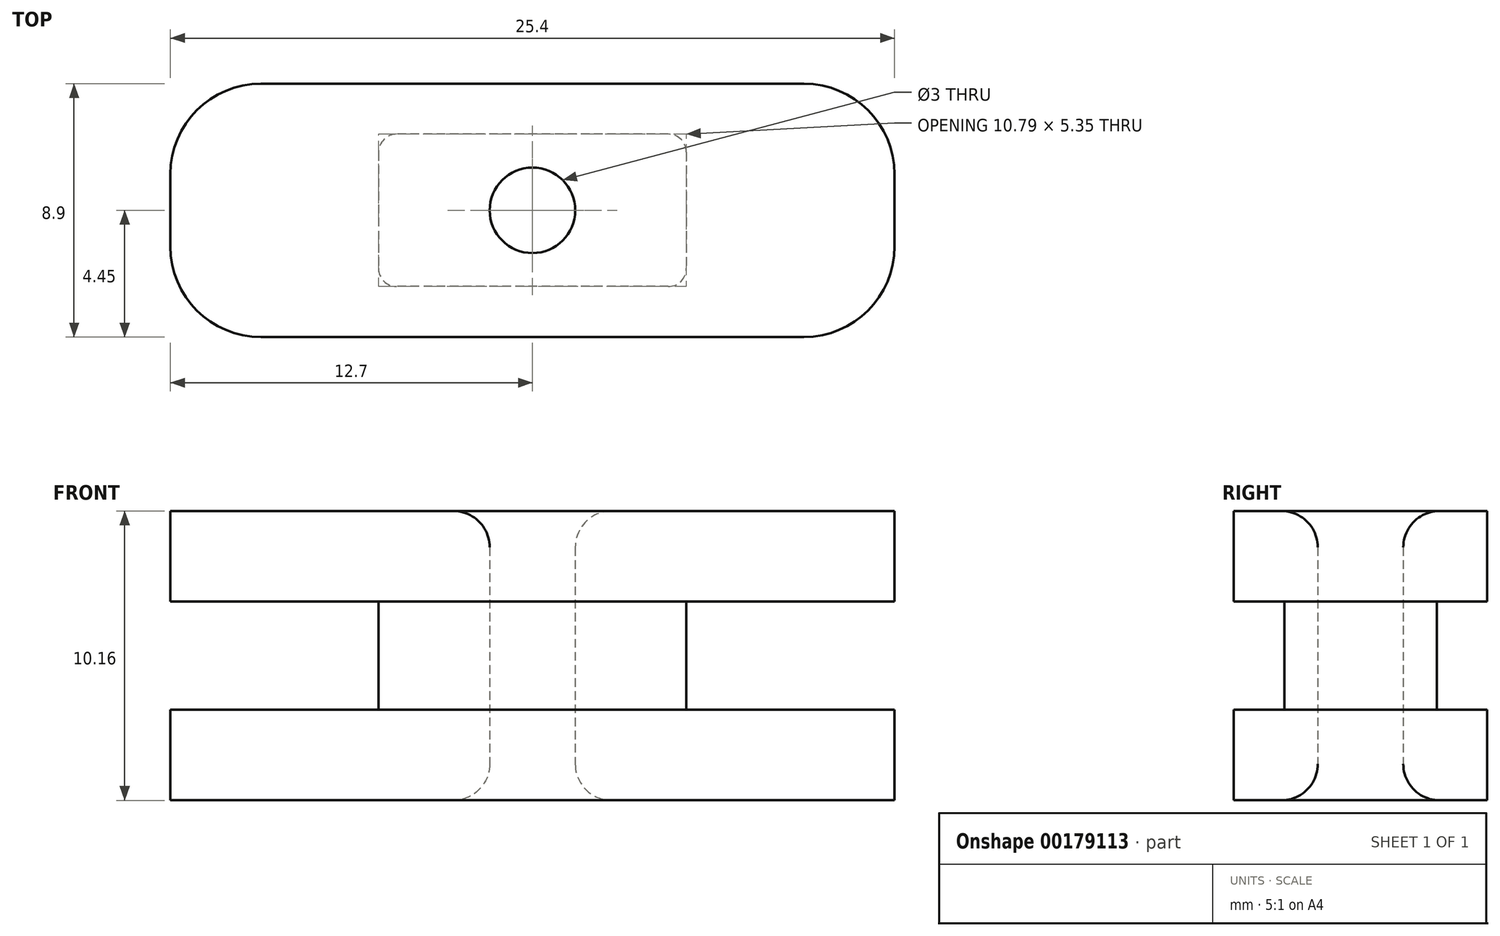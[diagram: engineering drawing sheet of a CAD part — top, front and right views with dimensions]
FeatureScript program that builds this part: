
annotation { "Feature Type Name" : "Feature", "Feature Type Description" : "" }
export const myFeature = defineFeature(function(context is Context, id is Id, definition is map)
    precondition{}
    {
        {
            var Q0;
            Q0=qCreatedBy(makeId("Top.planeOp"),FACE);
            var sketch = newSketch(context, id + "F0", { "sketchPlane" : qUnion([Q0])});
            skLineSegment(sketch, "E0.bottom", {"start": v(9.53, 4.45) * mm, "end": v(-9.53, 4.44) * mm});
            skLineSegment(sketch, "E0.top", {"start": v(9.53, -4.44) * mm, "end": v(-9.53, -4.45) * mm});
            skLineSegment(sketch, "E0.left", {"start": v(12.7, 1.27) * mm, "end": v(12.7, -1.27) * mm});
            skLineSegment(sketch, "E0.right", {"start": v(-12.7, 1.27) * mm, "end": v(-12.7, -1.27) * mm});
            skPoint(sketch, "E0.middle", {"position": v(0, 0) * mm});
            skLineSegment(sketch, "E1.bottom", {"start": v(4.76, 2.67) * mm, "end": v(-4.76, 2.67) * mm});
            skLineSegment(sketch, "E1.top", {"start": v(4.76, -2.67) * mm, "end": v(-4.76, -2.67) * mm});
            skLineSegment(sketch, "E1.left", {"start": v(5.4, 2.04) * mm, "end": v(5.4, -2.04) * mm});
            skLineSegment(sketch, "E1.right", {"start": v(-5.4, 2.04) * mm, "end": v(-5.4, -2.04) * mm});
            skPoint(sketch, "E2.visualSharp", {"position": v(-5.4, 2.67) * mm});
            skArc(sketch, "E2.filletArc", {"start": v(-4.76, 2.67) * mm, "mid": v(-5.21, 2.49) * mm, "end": v(-5.4, 2.04) * mm});
            skPoint(sketch, "E3.visualSharp", {"position": v(-5.4, -2.67) * mm});
            skArc(sketch, "E3.filletArc", {"start": v(-5.4, -2.04) * mm, "mid": v(-5.21, -2.49) * mm, "end": v(-4.76, -2.67) * mm});
            skPoint(sketch, "E4.visualSharp", {"position": v(5.4, -2.67) * mm});
            skArc(sketch, "E4.filletArc", {"start": v(4.76, -2.67) * mm, "mid": v(5.21, -2.49) * mm, "end": v(5.4, -2.04) * mm});
            skPoint(sketch, "E5.visualSharp", {"position": v(5.4, 2.67) * mm});
            skArc(sketch, "E5.filletArc", {"start": v(5.4, 2.04) * mm, "mid": v(5.21, 2.49) * mm, "end": v(4.76, 2.67) * mm});
            skCircle(sketch, "E6", {"center": v(0, 0) * mm, "radius": 1.5 * mm});
            skPoint(sketch, "E7.visualSharp", {"position": v(-12.7, 4.44) * mm});
            skArc(sketch, "E7.filletArc", {"start": v(-9.53, 4.44) * mm, "mid": v(-11.77, 3.52) * mm, "end": v(-12.7, 1.27) * mm});
            skPoint(sketch, "E8.visualSharp", {"position": v(-12.7, -4.45) * mm});
            skArc(sketch, "E8.filletArc", {"start": v(-12.7, -1.27) * mm, "mid": v(-11.77, -3.52) * mm, "end": v(-9.53, -4.45) * mm});
            skPoint(sketch, "E9.visualSharp", {"position": v(12.7, 4.45) * mm});
            skArc(sketch, "E9.filletArc", {"start": v(12.7, 1.27) * mm, "mid": v(11.77, 3.52) * mm, "end": v(9.53, 4.45) * mm});
            skPoint(sketch, "E10.visualSharp", {"position": v(12.7, -4.44) * mm});
            skArc(sketch, "E10.filletArc", {"start": v(9.53, -4.44) * mm, "mid": v(11.77, -3.52) * mm, "end": v(12.7, -1.27) * mm});
            skSolve(sketch);
        }
        {
            var Q0;
            Q0=makeQuery(id+"F0.imprint","IMPRINT",FACE,{"disambiguationData":[TD([[makeQuery(id+"F0.imprint","IMPRINT",EDGE,{"derivedFrom":sQuery(id+"F0.wireOp",EDGE,"E1.bottom")}),1.0]])]});
            extrude(context, id + "F1", {"entities" : qUnion([Q0]), "depth" : 3.8 * mm});
        }
        {
            var Q0;
            Q0 = qSketchRegion(id + "F0", true);
            var Q1;
            Q1=makeQuery(id+"F1.opExtrude","CAP_FACE",FACE,{"disambiguationData":[OSD([sQuery(id+"F0.wireOp",EDGE,"E1.bottom"),sQuery(id+"F0.wireOp",EDGE,"E1.top"),sQuery(id+"F0.wireOp",EDGE,"E1.left"),sQuery(id+"F0.wireOp",EDGE,"E1.right"),sQuery(id+"F0.wireOp",EDGE,"E2.filletArc"),sQuery(id+"F0.wireOp",EDGE,"E3.filletArc"),sQuery(id+"F0.wireOp",EDGE,"E4.filletArc"),sQuery(id+"F0.wireOp",EDGE,"E5.filletArc"),sQuery(id+"F0.wireOp",EDGE,"E6")])],"isStart":true});
            extrude(context, id + "F2", {"entities" : qUnion([Q0, Q1]), "operationType" : NewBodyOperationType.ADD, "oppositeDirection" : true, "depth" : 3.17 * mm});
        }
        {
            var Q0;
            Q0=makeQuery(id+"F1.opExtrude","CAP_FACE",FACE,{"disambiguationData":[OSD([sQuery(id+"F0.wireOp",EDGE,"E1.bottom"),sQuery(id+"F0.wireOp",EDGE,"E1.top"),sQuery(id+"F0.wireOp",EDGE,"E1.left"),sQuery(id+"F0.wireOp",EDGE,"E1.right"),sQuery(id+"F0.wireOp",EDGE,"E2.filletArc"),sQuery(id+"F0.wireOp",EDGE,"E3.filletArc"),sQuery(id+"F0.wireOp",EDGE,"E4.filletArc"),sQuery(id+"F0.wireOp",EDGE,"E5.filletArc"),sQuery(id+"F0.wireOp",EDGE,"E6")])],"isStart":false});
            var sketch = newSketch(context, id + "F3", { "sketchPlane" : qUnion([Q0])});
            skLineSegment(sketch, "E11.bottom", {"start": v(9.53, 4.44) * mm, "end": v(-9.53, 4.45) * mm});
            skLineSegment(sketch, "E11.top", {"start": v(9.53, -4.45) * mm, "end": v(-9.53, -4.45) * mm});
            skLineSegment(sketch, "E11.left", {"start": v(12.7, 1.27) * mm, "end": v(12.7, -1.27) * mm});
            skLineSegment(sketch, "E11.right", {"start": v(-12.7, 1.27) * mm, "end": v(-12.7, -1.27) * mm});
            skPoint(sketch, "E11.middle", {"position": v(0, 0) * mm});
            skCircle(sketch, "E12", {"center": v(0, 0) * mm, "radius": 1.5 * mm});
            skPoint(sketch, "E13.visualSharp", {"position": v(-12.7, 4.45) * mm});
            skArc(sketch, "E13.filletArc", {"start": v(-9.53, 4.45) * mm, "mid": v(-11.77, 3.52) * mm, "end": v(-12.7, 1.27) * mm});
            skPoint(sketch, "E14.visualSharp", {"position": v(-12.7, -4.44) * mm});
            skArc(sketch, "E14.filletArc", {"start": v(-12.7, -1.27) * mm, "mid": v(-11.77, -3.52) * mm, "end": v(-9.53, -4.45) * mm});
            skPoint(sketch, "E15.visualSharp", {"position": v(12.7, 4.44) * mm});
            skArc(sketch, "E15.filletArc", {"start": v(12.7, 1.27) * mm, "mid": v(11.77, 3.52) * mm, "end": v(9.53, 4.44) * mm});
            skPoint(sketch, "E16.visualSharp", {"position": v(12.7, -4.45) * mm});
            skArc(sketch, "E16.filletArc", {"start": v(9.53, -4.45) * mm, "mid": v(11.77, -3.52) * mm, "end": v(12.7, -1.27) * mm});
            skSolve(sketch);
        }
        {
            var Q0;
            Q0=makeQuery(id+"F3.imprint","IMPRINT",FACE,{"disambiguationData":[TD([[makeQuery(id+"F3.imprint","IMPRINT",EDGE,{"derivedFrom":sQuery(id+"F3.wireOp",EDGE,"E11.bottom")}),1.0]])]});
            var Q1;
            Q1=makeQuery(id+"F3.imprint","IMPRINT",FACE,{"disambiguationData":[TD([[makeQuery(id+"F3.imprint","IMPRINT",EDGE,{"derivedFrom":sQuery(id+"F3.wireOp",EDGE,"E12")}),-1.0]])]});
            extrude(context, id + "F4", {"entities" : qUnion([Q0, Q1]), "operationType" : NewBodyOperationType.ADD, "depth" : 3.17 * mm});
        }
        {
            var Q0;
            Q0=makeQuery(id+"F4.opExtrude","CAP_EDGE",EDGE,{"disambiguationData":[OSD([sQuery(id+"F3.wireOp",EDGE,"E12")])],"isStart":false});
            fillet(context, id + "F5", {"entities" : qUnion([Q0]), "radius" : 1.27 * mm, "tangentPropagation" : true, "allowEdgeOverflow" : false});
        }
        {
            var Q0;
            Q0=makeQuery(id+"F2.opExtrude","CAP_EDGE",EDGE,{"disambiguationData":[OSD([sQuery(id+"F0.wireOp",EDGE,"E6")])],"isStart":false});
            fillet(context, id + "F6", {"entities" : qUnion([Q0]), "radius" : 1.27 * mm, "tangentPropagation" : true, "allowEdgeOverflow" : false});
        }
    });
